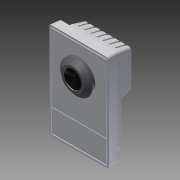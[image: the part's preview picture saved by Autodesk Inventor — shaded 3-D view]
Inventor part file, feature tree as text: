
AUTODESK INVENTOR PART (.ipt)
format: ipt  version: 2013 (Build 170138000, 138)  size: 774,144 bytes
history: native  units: in
note: dims shown in document units (in); Inventor stores cm internally (conversion verified against a paired STEP export)
features: fillet x1, other x1, imported_body x1
ambient origin geometry x8: Origin, YZ Plane, XZ Plane, XY Plane, X Axis, Y Axis, Z Axis, Center Point
feature tree (3):
  fillet  "Fillet18"  [1 undecoded]
  other  "AXIS M10111"
  imported_body  "Base1"
note: 1 required parameter value undecoded (feature->parameter linkage not recoverable at this tier; creation-order binding heuristic only, values carry confidence <= 0.55)
